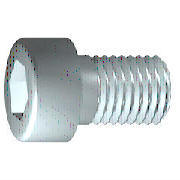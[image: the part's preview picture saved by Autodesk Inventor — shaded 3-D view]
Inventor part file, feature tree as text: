
AUTODESK INVENTOR PART (.ipt)
format: ipt  version: 2020 (Build 240168000, 168)  size: 191,488 bytes
history: native  units: mm (DEFAULTED — no unit token found)
features: sketch x2, other x1, extrude x1, plane x1, fillet x1
ambient origin geometry x7: Origin, YZ Plane, XY Plane, X Axis, Y Axis, Z Axis, Center Point
bodies: Solid1 (feature_tree)
feature tree (6):
  other  "Bryła"
  extrude  "Szczelina"  Depth=23.0mm
  plane  "Work Plane1"
  fillet  "Fillet2"  Radius=0.49086mm
  sketch  "Szkic1"
  sketch  "Szkic2"
